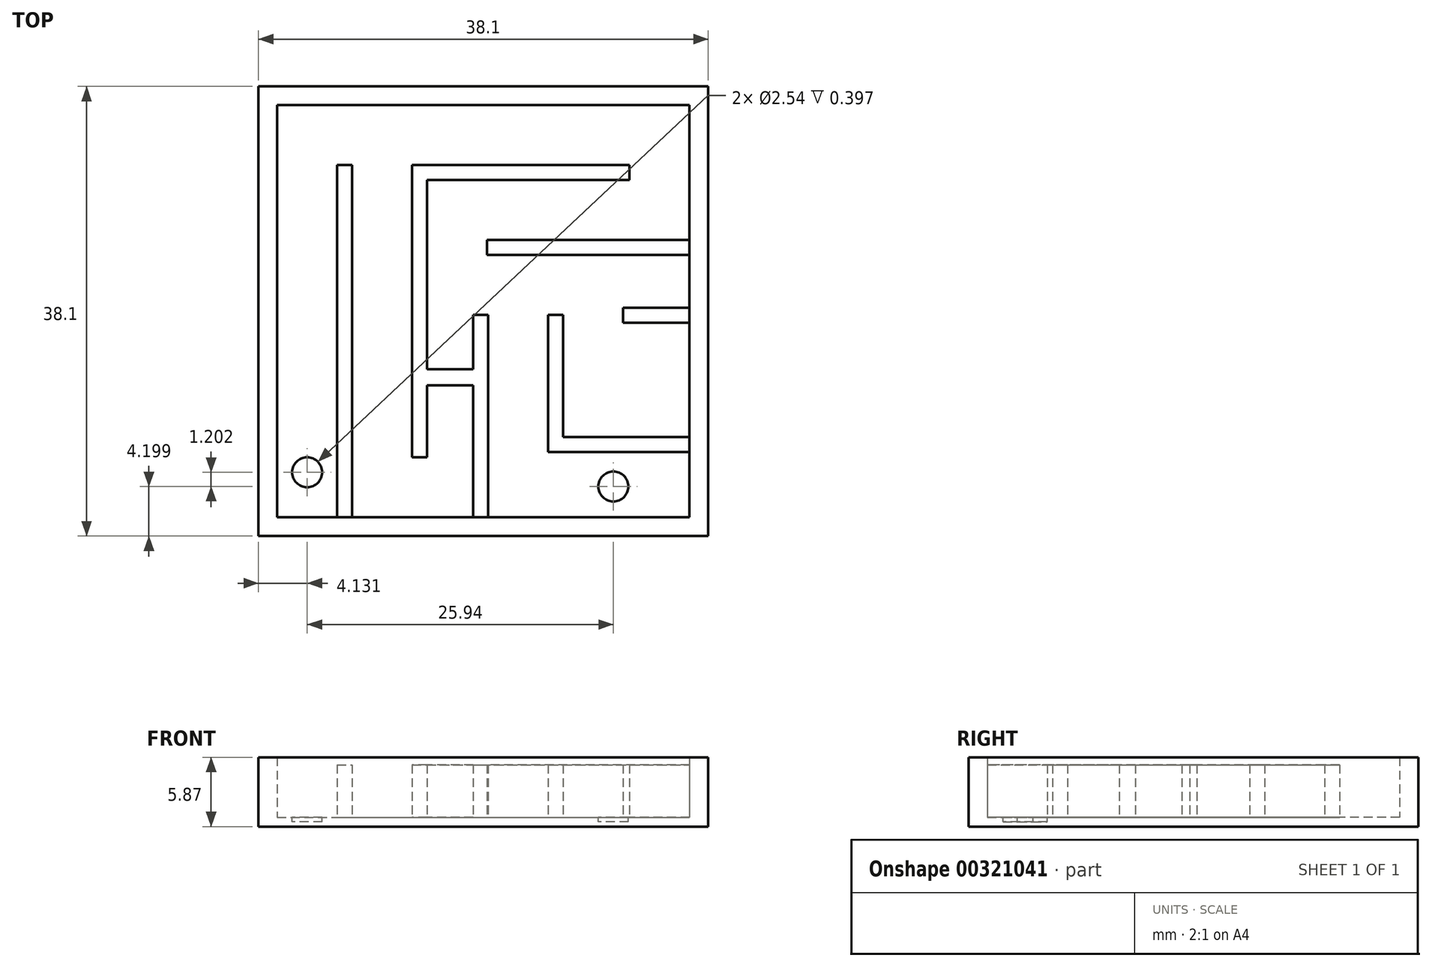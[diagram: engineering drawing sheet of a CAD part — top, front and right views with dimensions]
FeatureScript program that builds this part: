
annotation { "Feature Type Name" : "Feature", "Feature Type Description" : "" }
export const myFeature = defineFeature(function(context is Context, id is Id, definition is map)
    precondition{}
    {
        {
            var Q0;
            Q0=qCreatedBy(makeId("Top.planeOp"),FACE);
            var sketch = newSketch(context, id + "F0", { "sketchPlane" : qUnion([Q0])});
            skLineSegment(sketch, "E0.bottom", {"start": v(-23.76, 21.1) * mm, "end": v(14.34, 21.1) * mm});
            skLineSegment(sketch, "E0.top", {"start": v(-23.76, -17) * mm, "end": v(14.34, -17) * mm});
            skLineSegment(sketch, "E0.left", {"start": v(-23.76, 21.1) * mm, "end": v(-23.76, -17) * mm});
            skLineSegment(sketch, "E0.right", {"start": v(14.34, 21.1) * mm, "end": v(14.34, -17) * mm});
            skSolve(sketch);
        }
        {
            var Q0;
            Q0=makeQuery(id+"F0.imprint","IMPRINT",FACE,{"disambiguationData":[TD([[makeQuery(id+"F0.imprint","IMPRINT",EDGE,{"derivedFrom":sQuery(id+"F0.wireOp",EDGE,"E0.bottom")}),-1.0]])]});
            extrude(context, id + "F1", {"entities" : qUnion([Q0]), "depth" : 0.8 * mm});
        }
        {
            var Q0;
            Q0=makeQuery(id+"F1.opExtrude","CAP_FACE",FACE,{"disambiguationData":[OSD([sQuery(id+"F0.wireOp",EDGE,"E0.bottom"),sQuery(id+"F0.wireOp",EDGE,"E0.top"),sQuery(id+"F0.wireOp",EDGE,"E0.left"),sQuery(id+"F0.wireOp",EDGE,"E0.right")])],"isStart":false});
            var sketch = newSketch(context, id + "F2", { "sketchPlane" : qUnion([Q0])});
            skLineSegment(sketch, "E1.0", {"start": v(-22.17, 19.52) * mm, "end": v(12.76, 19.52) * mm});
            skLineSegment(sketch, "E1.1", {"start": v(-22.17, 19.52) * mm, "end": v(-22.17, -15.4) * mm});
            skLineSegment(sketch, "E1.2", {"start": v(-22.17, -15.4) * mm, "end": v(12.76, -15.4) * mm});
            skLineSegment(sketch, "E1.3", {"start": v(12.76, 19.52) * mm, "end": v(12.76, -15.4) * mm});
            skSolve(sketch);
        }
        {
            var Q0;
            Q0=makeQuery(id+"F2.imprint","IMPRINT",FACE,{"disambiguationData":[TD([[makeQuery(id+"F2.imprint","IMPRINT",EDGE,{"derivedFrom":sQuery(id+"F2.wireOp",EDGE,"E1.0")}),1.0]])]});
            extrude(context, id + "F3", {"entities" : qUnion([Q0]), "operationType" : NewBodyOperationType.ADD, "depth" : 5.08 * mm});
        }
        {
            var Q0;
            Q0=makeQuery(id+"F1.opExtrude","CAP_FACE",FACE,{"disambiguationData":[OSD([sQuery(id+"F0.wireOp",EDGE,"E0.bottom"),sQuery(id+"F0.wireOp",EDGE,"E0.top"),sQuery(id+"F0.wireOp",EDGE,"E0.left"),sQuery(id+"F0.wireOp",EDGE,"E0.right")])],"isStart":false});
            var sketch = newSketch(context, id + "F4", { "sketchPlane" : qUnion([Q0])});
            skLineSegment(sketch, "E2.bottom", {"start": v(-17.09, -15.4) * mm, "end": v(-15.82, -15.4) * mm});
            skLineSegment(sketch, "E2.top", {"start": v(-17.09, 14.44) * mm, "end": v(-15.82, 14.44) * mm});
            skLineSegment(sketch, "E2.left", {"start": v(-17.09, -15.4) * mm, "end": v(-17.09, 14.44) * mm});
            skLineSegment(sketch, "E2.right", {"start": v(-15.82, -15.4) * mm, "end": v(-15.82, 14.44) * mm});
            skLineSegment(sketch, "E3.bottom", {"start": v(-10.74, 19.52) * mm, "end": v(-9.47, 19.52) * mm});
            skLineSegment(sketch, "E4", {"start": v(-15.82, 4.6) * mm, "end": v(-15.82, 6.32) * mm});
            skLineSegment(sketch, "E5.trimOffspring", {"start": v(-10.74, 4.6) * mm, "end": v(-10.74, -10.33) * mm});
            skLineSegment(sketch, "E6.trimOffspring", {"start": v(-9.47, 4.6) * mm, "end": v(-9.47, -2.87) * mm});
            skLineSegment(sketch, "E7", {"start": v(-9.47, -10.33) * mm, "end": v(-10.74, -10.33) * mm});
            skLineSegment(sketch, "E8", {"start": v(-9.47, -2.87) * mm, "end": v(-5.57, -2.87) * mm});
            skLineSegment(sketch, "E9", {"start": v(-5.57, -4.22) * mm, "end": v(-9.47, -4.22) * mm});
            skLineSegment(sketch, "E10.trimOffspring", {"start": v(-9.47, -4.22) * mm, "end": v(-9.47, -10.33) * mm});
            skLineSegment(sketch, "E11", {"start": v(-10.74, 6.32) * mm, "end": v(-10.74, 4.6) * mm});
            skLineSegment(sketch, "E12", {"start": v(-9.47, 6.32) * mm, "end": v(-9.47, 4.6) * mm});
            skLineSegment(sketch, "E13", {"start": v(-10.74, 6.32) * mm, "end": v(-10.74, 14.44) * mm});
            skLineSegment(sketch, "E14", {"start": v(-10.74, 14.44) * mm, "end": v(-9.47, 14.44) * mm});
            skLineSegment(sketch, "E15", {"start": v(-9.47, 13.17) * mm, "end": v(-9.47, 6.32) * mm});
            skLineSegment(sketch, "E16", {"start": v(-22.17, -15.4) * mm, "end": v(-17.09, -15.4) * mm});
            skCircle(sketch, "E17", {"center": v(-19.63, -11.6) * mm, "radius": 1.27 * mm});
            skPoint(sketch, "E17.centerSnap0", {"position": v(-19.63, -15.4) * mm});
            skLineSegment(sketch, "E18", {"start": v(2.05, -9.87) * mm, "end": v(7.68, -9.87) * mm});
            skLineSegment(sketch, "E19", {"start": v(7.68, -8.6) * mm, "end": v(2.05, -8.6) * mm});
            skLineSegment(sketch, "E20", {"start": v(3.7, -15.4) * mm, "end": v(12.76, -15.4) * mm});
            skCircle(sketch, "E21", {"center": v(6.31, -12.8) * mm, "radius": 1.27 * mm});
            skLineSegment(sketch, "E22.top", {"start": v(-5.57, -15.4) * mm, "end": v(-4.3, -15.4) * mm});
            skLineSegment(sketch, "E22.left", {"start": v(-5.57, -4.22) * mm, "end": v(-5.57, -15.4) * mm});
            skLineSegment(sketch, "E22.right", {"start": v(-4.3, -2.87) * mm, "end": v(-4.3, -15.4) * mm});
            skLineSegment(sketch, "E23.bottom", {"start": v(-9.47, 14.44) * mm, "end": v(7.68, 14.44) * mm});
            skLineSegment(sketch, "E23.top", {"start": v(-9.47, 13.17) * mm, "end": v(7.68, 13.17) * mm});
            skLineSegment(sketch, "E23.right", {"start": v(7.68, 14.44) * mm, "end": v(7.68, 13.17) * mm});
            skLineSegment(sketch, "E24", {"start": v(-5.57, -2.87) * mm, "end": v(-5.57, 1.74) * mm});
            skLineSegment(sketch, "E25", {"start": v(-5.57, 1.74) * mm, "end": v(-4.3, 1.74) * mm});
            skLineSegment(sketch, "E26", {"start": v(-4.3, 1.74) * mm, "end": v(-4.3, -2.87) * mm});
            skLineSegment(sketch, "E27.top", {"start": v(12.76, 8.09) * mm, "end": v(-4.39, 8.09) * mm});
            skLineSegment(sketch, "E27.left", {"start": v(12.76, 6.82) * mm, "end": v(12.76, 8.09) * mm});
            skLineSegment(sketch, "E27.right", {"start": v(-4.39, 6.82) * mm, "end": v(-4.39, 8.09) * mm});
            skLineSegment(sketch, "E28.top", {"start": v(0.78, 1.74) * mm, "end": v(2.05, 1.74) * mm});
            skLineSegment(sketch, "E28.left", {"start": v(0.78, -9.87) * mm, "end": v(0.78, -5.34) * mm});
            skLineSegment(sketch, "E28.right", {"start": v(2.05, -8.6) * mm, "end": v(2.05, 1.74) * mm});
            skLineSegment(sketch, "E29", {"start": v(-4.39, 6.82) * mm, "end": v(12.76, 6.82) * mm});
            skLineSegment(sketch, "E30.bottom", {"start": v(12.76, 2.35) * mm, "end": v(7.13, 2.35) * mm});
            skLineSegment(sketch, "E30.top", {"start": v(12.76, 1.08) * mm, "end": v(7.13, 1.08) * mm});
            skLineSegment(sketch, "E30.left", {"start": v(12.76, 2.35) * mm, "end": v(12.76, 1.08) * mm});
            skLineSegment(sketch, "E30.right", {"start": v(7.13, 2.35) * mm, "end": v(7.13, 1.08) * mm});
            skLineSegment(sketch, "E31", {"start": v(0.78, -9.87) * mm, "end": v(0.78, -10.33) * mm});
            skLineSegment(sketch, "E32", {"start": v(2.05, -10.33) * mm, "end": v(2.05, -9.87) * mm});
            skLineSegment(sketch, "E33.bottom", {"start": v(0.78, -4.07) * mm, "end": v(0.78, -4.07) * mm});
            skLineSegment(sketch, "E33.top", {"start": v(0.78, -5.34) * mm, "end": v(0.78, -5.34) * mm});
            skLineSegment(sketch, "E33.right", {"start": v(0.78, -4.07) * mm, "end": v(0.78, -5.34) * mm});
            skLineSegment(sketch, "E34.trimOffspring", {"start": v(0.78, -4.07) * mm, "end": v(0.78, 1.74) * mm});
            skLineSegment(sketch, "E35", {"start": v(0.78, -9.87) * mm, "end": v(2.05, -9.87) * mm});
            skPoint(sketch, "E36.start.orphan", {"position": v(12.76, -8.6) * mm});
            skLineSegment(sketch, "E37", {"start": v(7.68, -8.6) * mm, "end": v(12.76, -8.6) * mm});
            skLineSegment(sketch, "E38", {"start": v(12.76, -8.6) * mm, "end": v(12.76, -9.87) * mm});
            skLineSegment(sketch, "E39", {"start": v(12.76, -9.87) * mm, "end": v(7.68, -9.87) * mm});
            skSolve(sketch);
        }
        {
            var Q0;
            Q0=makeQuery(id+"F4.imprint","IMPRINT",FACE,{"disambiguationData":[TD([[makeQuery(id+"F4.imprint","IMPRINT",EDGE,{"derivedFrom":sQuery(id+"F4.wireOp",EDGE,"E17")}),1.0]])]});
            var Q1;
            Q1=makeQuery(id+"F4.imprint","IMPRINT",FACE,{"disambiguationData":[TD([[makeQuery(id+"F4.imprint","IMPRINT",EDGE,{"derivedFrom":sQuery(id+"F4.wireOp",EDGE,"E21")}),1.0]])]});
            extrude(context, id + "F5", {"entities" : qUnion([Q0, Q1]), "operationType" : NewBodyOperationType.REMOVE, "oppositeDirection" : true, "depth" : 0.4 * mm});
        }
        {
            var Q0;
            {var subQ1=sQuery(id+"F4.wireOp",EDGE,"E2.bottom");Q0=makeQuery(id+"F4.imprint","IMPRINT",FACE,{"disambiguationData":[TD([[makeQuery(id+"F4.imprint","IMPRINT",EDGE,{"derivedFrom":subQ1}),1.0]])]});}
            var Q1;
            Q1=makeQuery(id+"F4.imprint","IMPRINT",FACE,{"disambiguationData":[TD([[makeQuery(id+"F4.imprint","IMPRINT",EDGE,{"derivedFrom":sQuery(id+"F4.wireOp",EDGE,"E5.trimOffspring")}),1.0]])]});
            var Q2;
            Q2=makeQuery(id+"F4.imprint","IMPRINT",FACE,{"disambiguationData":[TD([[makeQuery(id+"F4.imprint","IMPRINT",EDGE,{"derivedFrom":sQuery(id+"F4.wireOp",EDGE,"E27.top")}),1.0]])]});
            var Q3;
            Q3=makeQuery(id+"F4.imprint","IMPRINT",FACE,{"disambiguationData":[TD([[makeQuery(id+"F4.imprint","IMPRINT",EDGE,{"derivedFrom":sQuery(id+"F4.wireOp",EDGE,"E18")}),1.0]])]});
            var Q4;
            Q4=makeQuery(id+"F4.imprint","IMPRINT",FACE,{"disambiguationData":[TD([[makeQuery(id+"F4.imprint","IMPRINT",EDGE,{"derivedFrom":sQuery(id+"F4.wireOp",EDGE,"E30.bottom")}),1.0]])]});
            extrude(context, id + "F6", {"entities" : qUnion([Q0, Q1, Q2, Q3, Q4]), "operationType" : NewBodyOperationType.ADD, "depth" : 4.44 * mm});
        }
    });
